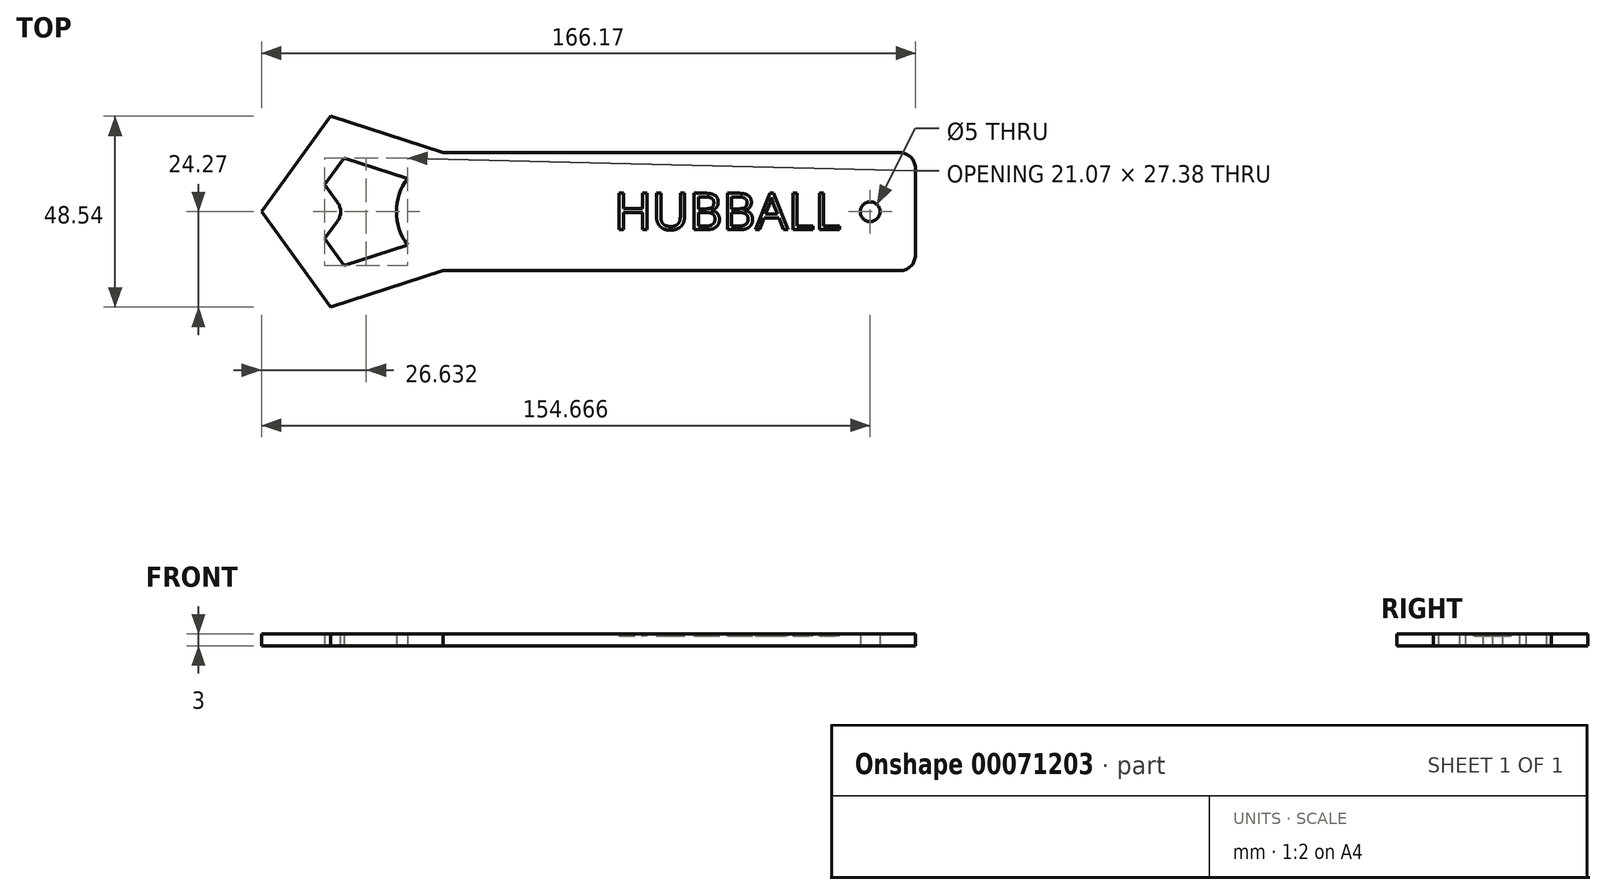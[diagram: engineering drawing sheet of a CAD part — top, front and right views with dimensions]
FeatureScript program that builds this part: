
annotation { "Feature Type Name" : "Feature", "Feature Type Description" : "" }
export const myFeature = defineFeature(function(context is Context, id is Id, definition is map)
    precondition{}
    {
        {
            var Q0;
            Q0=qCreatedBy(makeId("Top.planeOp"),FACE);
            var sketch = newSketch(context, id + "F0", { "sketchPlane" : qUnion([Q0])});
            skLineSegment(sketch, "E0.1", {"start": v(20.65, -15) * mm, "end": v(-7.89, -24.27) * mm});
            skLineSegment(sketch, "E0.2", {"start": v(-7.89, -24.27) * mm, "end": v(-25.52, 0) * mm});
            skLineSegment(sketch, "E0.3", {"start": v(-25.52, 0) * mm, "end": v(-7.89, 24.27) * mm});
            skLineSegment(sketch, "E0.4", {"start": v(-7.89, 24.27) * mm, "end": v(20.65, 15) * mm});
            skLineSegment(sketch, "E1.bottom", {"start": v(20.65, 15) * mm, "end": v(140.65, 15) * mm});
            skLineSegment(sketch, "E1.top", {"start": v(20.65, -15) * mm, "end": v(140.65, -15) * mm});
            skLineSegment(sketch, "E1.right", {"start": v(140.65, 15) * mm, "end": v(140.65, -15) * mm});
            skLineSegment(sketch, "E2.1", {"start": v(11.65, -8.46) * mm, "end": v(-4.45, -13.7) * mm});
            skLineSegment(sketch, "E2.3", {"start": v(-4.45, 13.7) * mm, "end": v(11.65, 8.46) * mm});
            skLineSegment(sketch, "E3", {"start": v(-9.42, -6.85) * mm, "end": v(-4.45, -13.7) * mm});
            skLineSegment(sketch, "E4", {"start": v(-9.42, 6.85) * mm, "end": v(-4.45, 13.7) * mm});
            skLineSegment(sketch, "E5", {"start": v(-4.45, 0) * mm, "end": v(-9.42, 6.85) * mm});
            skLineSegment(sketch, "E6", {"start": v(-4.45, 0) * mm, "end": v(-9.42, -6.85) * mm});
            skArc(sketch, "E7", {"start": v(11.65, 8.46) * mm, "mid": v(8.8, 0) * mm, "end": v(11.65, -8.46) * mm});
            skPoint(sketch, "E8.endSnap0", {"position": v(140.65, 0) * mm});
            skLineSegment(sketch, "E9.left", {"start": v(140.65, 0) * mm, "end": v(140.65, -3.78) * mm});
            skCircle(sketch, "E10", {"center": v(129.15, 0) * mm, "radius": 2.5 * mm});
            skSolve(sketch);
        }
        {
            var Q0;
            Q0 = qSketchRegion(id + "F0", true);
            extrude(context, id + "F1", {"entities" : qUnion([Q0]), "depth" : 3 * mm});
        }
        {
            var Q0;
            Q0=makeQuery(id+"F1.opExtrude","SWEPT_EDGE",EDGE,{"disambiguationData":[OSD([sQuery(id+"F0.wireOp",EDGE,"E1.top"),sQuery(id+"F0.wireOp",EDGE,"E1.right")])]});
            var Q1;
            Q1=makeQuery(id+"F1.opExtrude","SWEPT_EDGE",EDGE,{"disambiguationData":[OSD([sQuery(id+"F0.wireOp",EDGE,"E1.bottom"),sQuery(id+"F0.wireOp",EDGE,"E1.right")])]});
            var Q2;
            Q2=makeQuery(id+"F1.opExtrude","SWEPT_EDGE",EDGE,{"disambiguationData":[OSD([sQuery(id+"F0.wireOp",EDGE,"E5"),sQuery(id+"F0.wireOp",EDGE,"E6")])]});
            fillet(context, id + "F2", {"entities" : qUnion([Q0, Q1, Q2]), "radius" : 4 * mm, "tangentPropagation" : true, "allowEdgeOverflow" : false});
        }
        {
            var Q0;
            Q0=makeQuery(id+"F1.opExtrude","CAP_FACE",FACE,{"disambiguationData":[OSD([sQuery(id+"F0.wireOp",EDGE,"E0.1"),sQuery(id+"F0.wireOp",EDGE,"E0.2"),sQuery(id+"F0.wireOp",EDGE,"E0.3"),sQuery(id+"F0.wireOp",EDGE,"E0.4"),sQuery(id+"F0.wireOp",EDGE,"E1.bottom"),sQuery(id+"F0.wireOp",EDGE,"E1.top"),sQuery(id+"F0.wireOp",EDGE,"E1.right"),sQuery(id+"F0.wireOp",EDGE,"E2.1"),sQuery(id+"F0.wireOp",EDGE,"E2.3"),sQuery(id+"F0.wireOp",EDGE,"E3"),sQuery(id+"F0.wireOp",EDGE,"E4"),sQuery(id+"F0.wireOp",EDGE,"E5"),sQuery(id+"F0.wireOp",EDGE,"E6"),sQuery(id+"F0.wireOp",EDGE,"E7"),sQuery(id+"F0.wireOp",EDGE,"E9.left"),sQuery(id+"F0.wireOp",EDGE,"E10")])],"isStart":false});
            var sketch = newSketch(context, id + "F3", { "sketchPlane" : qUnion([Q0])});
            skText(sketch, "E11", { "text": "HUBBALL", "fontName": "OpenSans-Regular.ttf"});
            const initialGuessF3  = {"E11": [0.06413, -0.00457, 1, 0, 0.00935]};
            skSetInitialGuess(sketch, initialGuessF3);
            skSolve(sketch);
        }
        {
            var Q0;
            Q0 = qSketchRegion(id + "F3", true);
            extrude(context, id + "F4", {"entities" : qUnion([Q0]), "operationType" : NewBodyOperationType.REMOVE, "oppositeDirection" : true, "depth" : 0.5 * mm});
        }
    });
